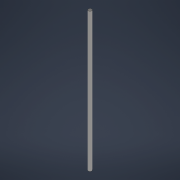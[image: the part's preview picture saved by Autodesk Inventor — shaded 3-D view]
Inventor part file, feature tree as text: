
AUTODESK INVENTOR PART (.ipt)
format: ipt  version: 2021 (Build 250183000, 183)  size: 83,456 bytes
history: native  units: mm
features: extrude x1, sketch x1
ambient origin geometry x8: Origin, YZ Plane, XZ Plane, XY Plane, X Axis, Y Axis, Z Axis, Center Point
bodies: Solid1 (feature_tree)
feature tree (2):
  extrude  "Extrusion1"  Depth=330.0mm TaperAngle=0.0deg
  sketch  "Sketch1"  dims[d0=8.0mm d1=330.0mm d2=0.0mm]
